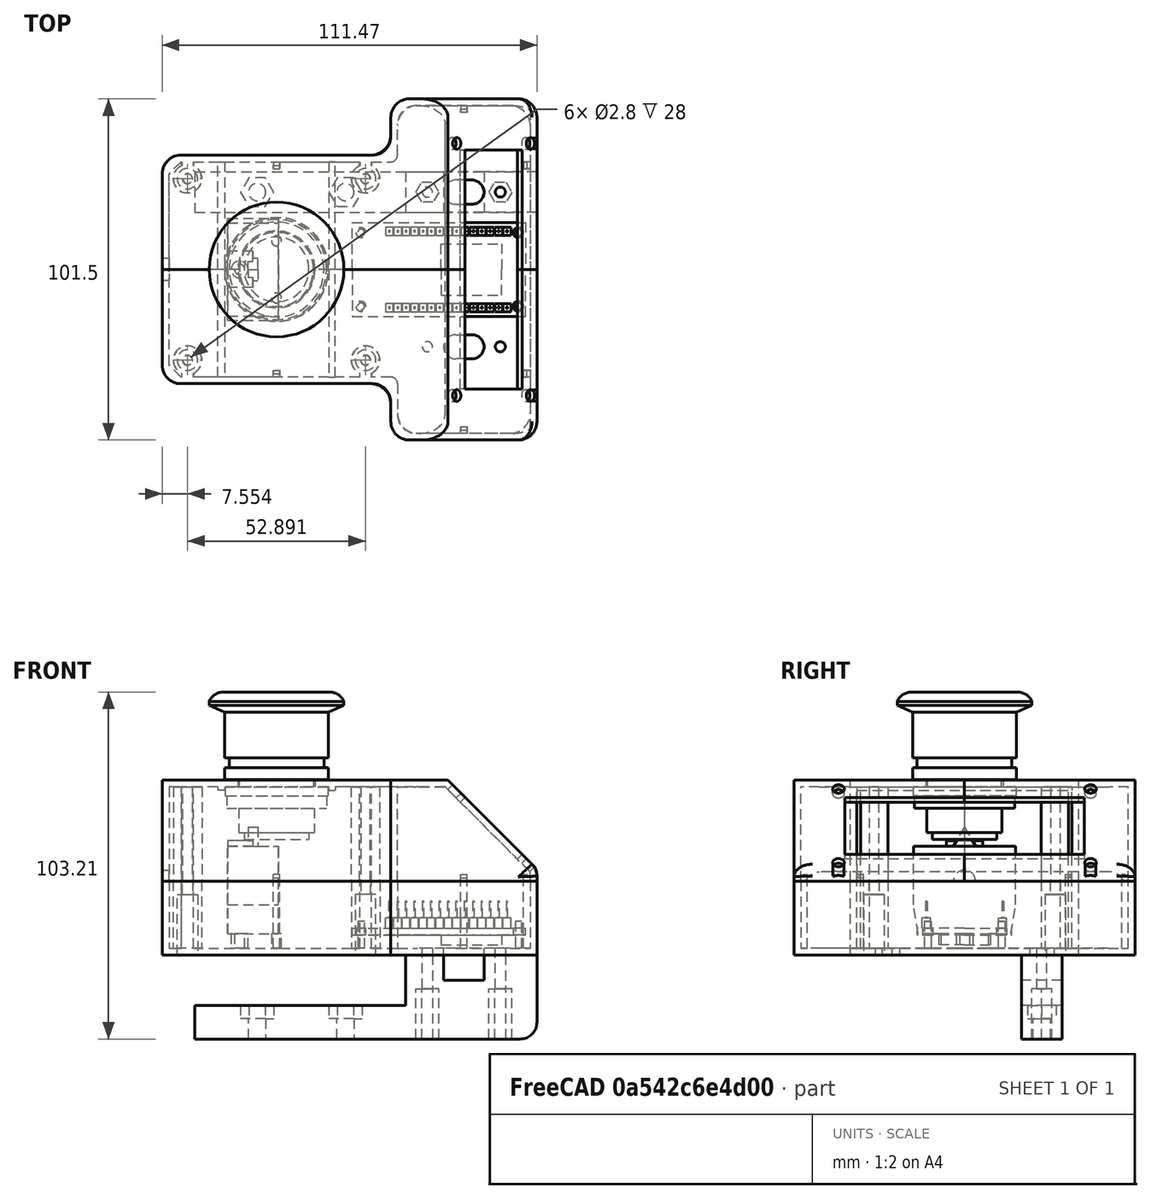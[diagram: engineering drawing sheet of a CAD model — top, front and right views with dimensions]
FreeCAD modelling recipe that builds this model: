
FCSTD DOCUMENT  (FreeCAD 0.21R33771 (Git))
Label: emergencybuttonv
License: All rights reserved
LicenseURL: https://en.wikipedia.org/wiki/All_rights_reserved
objects: Sketcher::SketchObject×35, PartDesign::Pad×16, PartDesign::Pocket×14, PartDesign::Mirrored×11, PartDesign::Body×6, PartDesign::Fillet×4, PartDesign::MultiTransform×3, Image::ImagePlane×3, PartDesign::Chamfer×3, PartDesign::Thickness×2, Mesh::Feature×1, PartDesign::Plane×1, PartDesign::Revolution×1, App::Link×1, Part::Compound×1, Part::Box×1, Part::Cut×1, PartDesign::LinearPattern×1
note: 140 computed .brp shape members not serialized (recipe doc carries the construction recipe); baked Part::Feature solids carry a one-line shape summary decoded from their .brp

FEATURE [Sketcher::SketchObject] Sketch
  FullyConstrained = false
  MapMode = 5
  Support = -> [XY_Plane]
  sketch-geometry (8):
    g0: LineSegment StartX=-34 StartY=34 StartZ=0 EndX=34 EndY=34 EndZ=0
    g1: LineSegment StartX=34 StartY=-34 StartZ=0 EndX=-34 EndY=-34 EndZ=0
    g2: LineSegment StartX=-34 StartY=-34 StartZ=0 EndX=-34 EndY=34 EndZ=0
    g3: LineSegment StartX=34 StartY=50.7535 StartZ=0 EndX=77.4691 EndY=50.7535 EndZ=0
    g4: LineSegment StartX=77.4691 StartY=50.7535 StartZ=0 EndX=77.4691 EndY=-50.7535 EndZ=0
    g5: LineSegment StartX=77.4691 StartY=-50.7535 StartZ=0 EndX=34 EndY=-50.7535 EndZ=0
    g6: LineSegment StartX=34 StartY=34 StartZ=0 EndX=34 EndY=50.7535 EndZ=0
    g7: LineSegment StartX=34 StartY=-34 StartZ=0 EndX=34 EndY=-50.7535 EndZ=0
  constraints (21):
    c: Coincident(g1,g2)
    c: Coincident(g2,g0)
    c: Horizontal(g0)
    c: Horizontal(g1)
    c: Vertical(g2)
    c: Coincident(g3,g4)
    c: Coincident(g4,g5)
    c: Horizontal(g3)
    c: Horizontal(g5)
    c: Vertical(g4)
    c: Coincident(g6,g0)
    c: Coincident(g6,g3)
    c: Vertical(g6)
    c: Coincident(g7,g1)
    c: Coincident(g7,g5)
    c: Vertical(g7)
    c: Equal(g6,g7)
    c: Symmetric(g1,g0,g-1)
    c: DistanceY(g2,g2) = 68
    c: Equal(g1,g2)
    c: Equal(g3,g5)
FEATURE [Mesh::Feature] LCD_16x2_I2C
  Placement = pos=(78,-89.5,-7) rot=(0,1,0;-0.785398rad)
FEATURE [PartDesign::Pad] Pad
  Direction = (0,0,1)
  Length = 30
  Length2 = 10
  Profile = -> Sketch
  ReferenceAxis = -> Sketch [N_Axis]
  Type = 0
FEATURE [PartDesign::Plane] DatumPlane
  AttachmentOffset = pos=(0,0,81) rot=(0,1,0;0.785398rad)
  Length = 152.683
  MapMode = 2
  Placement = pos=(0,0,81) rot=(0,1,0;0.785398rad)
  ResizeMode = 0
  Support = -> [XY_Plane]
  Width = 124.458
FEATURE [Sketcher::SketchObject] Sketch001
  FullyConstrained = false
  MapMode = 5
  Placement = pos=(0,0,81) rot=(0,1,0;0.785398rad)
  Support = -> [DatumPlane]
  sketch-geometry (4):
    g0: LineSegment StartX=17.5972 StartY=73.2272 StartZ=0 EndX=157.297 EndY=73.2272 EndZ=0
    g1: LineSegment StartX=157.297 StartY=73.2272 StartZ=0 EndX=157.297 EndY=-69.4661 EndZ=0
    g2: LineSegment StartX=157.297 StartY=-69.4661 StartZ=0 EndX=17.5972 EndY=-69.4661 EndZ=0
    g3: LineSegment StartX=17.5972 StartY=-69.4661 StartZ=0 EndX=17.5972 EndY=73.2272 EndZ=0
  constraints (8):
    c: Coincident(g0,g1)
    c: Coincident(g1,g2)
    c: Coincident(g2,g3)
    c: Coincident(g3,g0)
    c: Horizontal(g0)
    c: Horizontal(g2)
    c: Vertical(g1)
    c: Vertical(g3)
FEATURE [PartDesign::Pocket] Pocket
  BaseFeature = -> Pad
  Direction = (-0.707107,0,-0.707107)
  Length = 20
  Length2 = 5
  Profile = -> Sketch001
  ReferenceAxis = -> Sketch001 [N_Axis]
  Reversed = true
  Type = 0
FEATURE [PartDesign::Thickness] Thickness
  Base = -> Pocket [Face4]
  BaseFeature = -> Pocket
  Intersection = true
  Join = 0
  Mode = 0
  Reversed = true
  SupportTransform = false
  Value = 2
FEATURE [Sketcher::SketchObject] Sketch002
  FullyConstrained = false
  MapMode = 5
  Placement = pos=(0,0,81) rot=(0,1,0;0.785398rad)
  Support = -> [DatumPlane]
  sketch-geometry (4):
    g0: LineSegment StartX=79.3483 StartY=35.5767 StartZ=0 EndX=103.355 EndY=35.5767 EndZ=0
    g1: LineSegment StartX=103.355 StartY=35.5767 StartZ=0 EndX=103.355 EndY=-35.5767 EndZ=0
    g2: LineSegment StartX=103.355 StartY=-35.5767 StartZ=0 EndX=79.3483 EndY=-35.5767 EndZ=0
    g3: LineSegment StartX=79.3483 StartY=-35.5767 StartZ=0 EndX=79.3483 EndY=35.5767 EndZ=0
  constraints (8):
    c: Coincident(g0,g1)
    c: Coincident(g1,g2)
    c: Coincident(g2,g3)
    c: Coincident(g3,g0)
    c: Horizontal(g0)
    c: Horizontal(g2)
    c: Vertical(g1)
    c: Symmetric(g0,g2,g-1)
FEATURE [PartDesign::Pocket] Pocket001
  BaseFeature = -> Thickness
  Direction = (-0.707107,0,-0.707107)
  Length = 5
  Length2 = 5
  Profile = -> Sketch002
  ReferenceAxis = -> Sketch002 [N_Axis]
  Type = 0
FEATURE [Sketcher::SketchObject] Sketch003
  FullyConstrained = false
  MapMode = 5
  Placement = pos=(0,0,81) rot=(0,1,0;0.785398rad)
  Support = -> [DatumPlane]
  sketch-geometry (8):
    g0: LineSegment StartX=75.8332 StartY=37.5039 StartZ=0 EndX=106.819 EndY=37.5039 EndZ=0
    g1: LineSegment StartX=106.819 StartY=37.5039 StartZ=0 EndX=106.819 EndY=-37.5039 EndZ=0
    g2: LineSegment StartX=106.819 StartY=-37.5039 StartZ=0 EndX=75.8332 EndY=-37.5039 EndZ=0
    g3: LineSegment StartX=75.8332 StartY=-37.5039 StartZ=0 EndX=75.8332 EndY=37.5039 EndZ=0
    g4: Circle CenterX=75.8332 CenterY=37.5039 CenterZ=0 NormalX=0 NormalY=0 NormalZ=1 AngleXU=0 Radius=1.73847
    g5: Circle CenterX=106.819 CenterY=37.5039 CenterZ=0 NormalX=0 NormalY=0 NormalZ=1 AngleXU=0 Radius=1.73847
    g6: Circle CenterX=106.819 CenterY=-37.5039 CenterZ=0 NormalX=0 NormalY=0 NormalZ=1 AngleXU=0 Radius=1.73847
    g7: Circle CenterX=75.8332 CenterY=-37.5039 CenterZ=0 NormalX=0 NormalY=0 NormalZ=1 AngleXU=0 Radius=1.73847
  constraints (15):
    c: Coincident(g0,g1)
    c: Coincident(g1,g2)
    c: Coincident(g2,g3)
    c: Coincident(g3,g0)
    c: Horizontal(g0)
    c: Horizontal(g2)
    c: Vertical(g1)
    c: Symmetric(g2,g0,g-1)
    c: Coincident(g4,g0)
    c: Coincident(g5,g0)
    c: Coincident(g6,g1)
    c: Coincident(g7,g2)
    c: Equal(g4,g5)
    c: Equal(g5,g6)
    c: Equal(g6,g7)
FEATURE [PartDesign::Pocket] Pocket002
  BaseFeature = -> Pocket001
  Direction = (-0.707107,0,-0.707107)
  Length = 7
  Length2 = 5
  Profile = -> Sketch003
  ReferenceAxis = -> Sketch003 [N_Axis]
  Type = 0
FEATURE [Sketcher::SketchObject] Sketch004
  FullyConstrained = true
  MapMode = 5
  Support = -> [XY_Plane]
  sketch-geometry (1):
    g0: Circle CenterX=0 CenterY=0 CenterZ=0 NormalX=0 NormalY=0 NormalZ=1 AngleXU=0 Radius=11
  constraints (2):
    c: Coincident(g0,g-1)
    c: Diameter(g0) = 22
FEATURE [PartDesign::Pocket] Pocket003
  BaseFeature = -> Pocket002
  Direction = (0,0,-1)
  Length = 5
  Length2 = 5
  Midplane = true
  Profile = -> Sketch004
  ReferenceAxis = -> Sketch004 [N_Axis]
  Type = 1
FEATURE [Sketcher::SketchObject] Sketch005
  ExternalGeometry = -> [Sketch]
  FullyConstrained = false
  MapMode = 5
  Support = -> [XY_Plane]
  sketch-geometry (4):
    g0: LineSegment StartX=24.6956 StartY=32 StartZ=0 EndX=28.1956 EndY=32 EndZ=0
    g1: LineSegment StartX=28.1956 StartY=32 StartZ=0 EndX=28.1956 EndY=30.873 EndZ=0
    g2: LineSegment StartX=24.6956 StartY=30.873 StartZ=0 EndX=24.6956 EndY=32 EndZ=0
    g3: ArcOfCircle CenterX=26.4456 CenterY=27 CenterZ=0 NormalX=0 NormalY=0 NormalZ=1 AngleXU=0 Radius=4.25 StartAngle=1.99519 EndAngle=7.42959
  constraints (12):
    c: Coincident(g0,g1)
    c: Coincident(g2,g0)
    c: Horizontal(g0)
    c: Vertical(g1)
    c: Vertical(g2)
    c: Coincident(g3,g2)
    c: Coincident(g3,g1)
    c: Equal(g1,g2)
    c: Diameter(g3) = 8.5
    c: Distance(g0) = 3.5
    c: DistanceY(g3,g0) = 5
    c: DistanceY(g0,g-3) = 2
FEATURE [PartDesign::Pad] Pad001
  BaseFeature = -> Pocket003
  Direction = (0,0,1)
  Length = 28
  Length2 = 10
  Profile = -> Sketch005
  ReferenceAxis = -> Sketch005 [N_Axis]
  Type = 0
FEATURE [Sketcher::SketchObject] Sketch006
  ExternalGeometry = -> [Sketch005]
  FullyConstrained = true
  MapMode = 5
  Support = -> [XY_Plane]
  sketch-geometry (1):
    g0: Circle CenterX=26.4456 CenterY=27 CenterZ=0 NormalX=0 NormalY=0 NormalZ=1 AngleXU=0 Radius=1.4
  constraints (2):
    c: Coincident(g0,g-3)
    c: Diameter(g0) = 2.8
FEATURE [PartDesign::Pocket] Pocket004
  BaseFeature = -> Pad001
  Direction = (0,0,-1)
  Length = 28
  Length2 = 5
  Profile = -> Sketch006
  ReferenceAxis = -> Sketch006 [N_Axis]
  Reversed = true
  Type = 0
FEATURE [PartDesign::Mirrored] Mirrored
  MirrorPlane = -> Sketch006 [V_Axis]
FEATURE [PartDesign::Mirrored] Mirrored001
  MirrorPlane = -> Sketch006 [H_Axis]
FEATURE [PartDesign::MultiTransform] MultiTransform
  BaseFeature = -> Pocket004
  Originals = -> [Pad001,Pocket004]
  Transformations = -> [Mirrored,Mirrored001]
FEATURE [Sketcher::SketchObject] Sketch007
  FullyConstrained = false
  MapMode = 5
  Support = -> [XY_Plane001]
  sketch-geometry (8):
    g0: LineSegment StartX=-34 StartY=34 StartZ=0 EndX=34 EndY=34 EndZ=0
    g1: LineSegment StartX=34 StartY=-34 StartZ=0 EndX=-34 EndY=-34 EndZ=0
    g2: LineSegment StartX=-34 StartY=-34 StartZ=0 EndX=-34 EndY=34 EndZ=0
    g3: LineSegment StartX=34 StartY=50.7535 StartZ=0 EndX=77.4691 EndY=50.7535 EndZ=0
    g4: LineSegment StartX=77.4691 StartY=50.7535 StartZ=0 EndX=77.4691 EndY=-50.7535 EndZ=0
    g5: LineSegment StartX=77.4691 StartY=-50.7535 StartZ=0 EndX=34 EndY=-50.7535 EndZ=0
    g6: LineSegment StartX=34 StartY=34 StartZ=0 EndX=34 EndY=50.7535 EndZ=0
    g7: LineSegment StartX=34 StartY=-34 StartZ=0 EndX=34 EndY=-50.7535 EndZ=0
  constraints (21):
    c: Coincident(g1,g2)
    c: Coincident(g2,g0)
    c: Horizontal(g0)
    c: Horizontal(g1)
    c: Vertical(g2)
    c: Coincident(g3,g4)
    c: Coincident(g4,g5)
    c: Horizontal(g3)
    c: Horizontal(g5)
    c: Vertical(g4)
    c: Coincident(g6,g0)
    c: Coincident(g6,g3)
    c: Vertical(g6)
    c: Coincident(g7,g1)
    c: Coincident(g7,g5)
    c: Vertical(g7)
    c: Equal(g6,g7)
    c: Symmetric(g1,g0,g-1)
    c: DistanceY(g2,g2) = 68
    c: Equal(g1,g2)
    c: Equal(g3,g5)
FEATURE [PartDesign::Pad] Pad002
  Direction = (0,0,1)
  Length = 22
  Length2 = 10
  Profile = -> Sketch007
  ReferenceAxis = -> Sketch007 [N_Axis]
  Type = 0
FEATURE [Sketcher::SketchObject] Sketch012
  ExternalGeometry = -> [Sketch007]
  FullyConstrained = false
  MapMode = 5
  Support = -> [XY_Plane001]
  sketch-geometry (4):
    g0: LineSegment StartX=24.7653 StartY=32 StartZ=0 EndX=28.2653 EndY=32 EndZ=0
    g1: LineSegment StartX=28.2653 StartY=32 StartZ=0 EndX=28.2653 EndY=30.873 EndZ=0
    g2: LineSegment StartX=24.7653 StartY=30.873 StartZ=0 EndX=24.7653 EndY=32 EndZ=0
    g3: ArcOfCircle CenterX=26.5153 CenterY=27 CenterZ=0 NormalX=0 NormalY=0 NormalZ=1 AngleXU=0 Radius=4.25 StartAngle=1.99519 EndAngle=7.42959
  constraints (12):
    c: Coincident(g0,g1)
    c: Coincident(g2,g0)
    c: Horizontal(g0)
    c: Vertical(g1)
    c: Vertical(g2)
    c: Coincident(g3,g2)
    c: Coincident(g3,g1)
    c: Equal(g1,g2)
    c: Diameter(g3) = 8.5
    c: Distance(g0) = 3.5
    c: DistanceY(g3,g0) = 5
    c: DistanceY(g0,g-3) = 2
FEATURE [Sketcher::SketchObject] Sketch013
  ExternalGeometry = -> [Sketch012]
  FullyConstrained = true
  MapMode = 5
  Support = -> [XY_Plane001]
  sketch-geometry (1):
    g0: Circle CenterX=26.5153 CenterY=27 CenterZ=0 NormalX=0 NormalY=0 NormalZ=1 AngleXU=0 Radius=1.5
  constraints (2):
    c: Coincident(g0,g-3)
    c: Diameter(g0) = 3
FEATURE [PartDesign::Thickness] Thickness001
  Base = -> Pad002 [Face10]
  BaseFeature = -> Pad002
  Intersection = true
  Join = 0
  Mode = 0
  Reversed = true
  SupportTransform = false
  Value = 2
FEATURE [PartDesign::Pad] Pad003
  BaseFeature = -> Thickness001
  Direction = (0,0,1)
  Length = 22
  Length2 = 10
  Profile = -> Sketch012
  ReferenceAxis = -> Sketch012 [N_Axis]
  Type = 0
FEATURE [PartDesign::Pocket] Pocket009
  BaseFeature = -> Pad003
  Direction = (0,0,-1)
  Length = 32
  Length2 = 5
  Profile = -> Sketch013
  ReferenceAxis = -> Sketch013 [N_Axis]
  Reversed = true
  Type = 0
FEATURE [Sketcher::SketchObject] Sketch014
  ExternalGeometry = -> [Sketch012]
  FullyConstrained = true
  MapMode = 5
  Support = -> [XY_Plane001]
  sketch-geometry (1):
    g0: Circle CenterX=26.5153 CenterY=27 CenterZ=0 NormalX=0 NormalY=0 NormalZ=1 AngleXU=0 Radius=3.05
  constraints (2):
    c: Coincident(g0,g-3)
    c: Diameter(g0) = 6.1
FEATURE [PartDesign::Pocket] Pocket010
  BaseFeature = -> Pocket009
  Direction = (0,0,-1)
  Length = 18
  Length2 = 5
  Profile = -> Sketch014
  ReferenceAxis = -> Sketch014 [N_Axis]
  Reversed = true
  Type = 0
FEATURE [PartDesign::Mirrored] Mirrored002
  MirrorPlane = -> Sketch012 [V_Axis]
FEATURE [PartDesign::Mirrored] Mirrored003
  MirrorPlane = -> Sketch012 [H_Axis]
FEATURE [PartDesign::MultiTransform] MultiTransform001
  BaseFeature = -> Pocket010
  Originals = -> [Pad003,Pocket009,Pocket010]
  Transformations = -> [Mirrored002,Mirrored003]
FEATURE [Sketcher::SketchObject] Sketch015
  FullyConstrained = true
  MapMode = 5
  Support = -> [XY_Plane001]
  sketch-geometry (5):
    g0: Circle CenterX=0 CenterY=0 CenterZ=0 NormalX=0 NormalY=0 NormalZ=1 AngleXU=0 Radius=11
    g1: Circle CenterX=-11 CenterY=0 CenterZ=0 NormalX=0 NormalY=0 NormalZ=1 AngleXU=0 Radius=1.5
    g2: Circle CenterX=-11 CenterY=0 CenterZ=0 NormalX=0 NormalY=0 NormalZ=1 AngleXU=0 Radius=2.5
    g3: Circle CenterX=9e-16 CenterY=8.5 CenterZ=0 NormalX=0 NormalY=0 NormalZ=1 AngleXU=0 Radius=1.5
    g4: Circle CenterX=9e-16 CenterY=-8.5 CenterZ=0 NormalX=0 NormalY=0 NormalZ=1 AngleXU=0 Radius=1.5
  constraints (12):
    c: Coincident(g0,g-1)
    c: Diameter(g0) = 22
    c: PointOnObject(g1,g0)
    c: PointOnObject(g1,g-1)
    c: Coincident(g2,g1)
    c: Diameter(g1) = 3
    c: Diameter(g2) = 5
    c: Symmetric(g4,g3,g-1)
    c: Equal(g3,g4)
    c: Equal(g4,g1)
    c: DistanceX(g1,g4) = 11
    c: DistanceY(g4,g3) = 17
FEATURE [PartDesign::Pad] Pad004
  BaseFeature = -> MultiTransform001
  Direction = (0,0,1)
  Length = 6.3
  Length2 = 10
  Profile = -> Sketch015
  ReferenceAxis = -> Sketch015 [N_Axis]
  Type = 0
FEATURE [Sketcher::SketchObject] Sketch016
  ExternalGeometry = -> [Sketch007]
  FullyConstrained = true
  MapMode = 5
  Support = -> [XY_Plane001]
  sketch-geometry (12):
    g0: LineSegment StartX=-1 StartY=32 StartZ=0 EndX=1 EndY=32 EndZ=0
    g1: LineSegment StartX=1 StartY=32 StartZ=0 EndX=1 EndY=30 EndZ=0
    g2: LineSegment StartX=1 StartY=30 StartZ=0 EndX=-1 EndY=30 EndZ=0
    g3: LineSegment StartX=-1 StartY=30 StartZ=0 EndX=-1 EndY=32 EndZ=0
    g4: LineSegment StartX=54.7341 StartY=48.7535 StartZ=0 EndX=56.7341 EndY=48.7535 EndZ=0
    g5: LineSegment StartX=56.7341 StartY=48.7535 StartZ=0 EndX=56.7341 EndY=46.7535 EndZ=0
    g6: LineSegment StartX=56.7341 StartY=46.7535 StartZ=0 EndX=54.7341 EndY=46.7535 EndZ=0
    g7: LineSegment StartX=54.7341 StartY=46.7535 StartZ=0 EndX=54.7341 EndY=48.7535 EndZ=0
    g8: LineSegment StartX=73.4691 StartY=32 StartZ=0 EndX=75.4691 EndY=32 EndZ=0
    g9: LineSegment StartX=75.4691 StartY=32 StartZ=0 EndX=75.4691 EndY=30 EndZ=0
    g10: LineSegment StartX=75.4691 StartY=30 StartZ=0 EndX=73.4691 EndY=30 EndZ=0
    g11: LineSegment StartX=73.4691 StartY=30 StartZ=0 EndX=73.4691 EndY=32 EndZ=0
  constraints (36):
    c: Coincident(g0,g1)
    c: Coincident(g1,g2)
    c: Coincident(g2,g3)
    c: Coincident(g3,g0)
    c: Horizontal(g0)
    c: Vertical(g1)
    c: Vertical(g3)
    c: Coincident(g4,g5)
    c: Coincident(g5,g6)
    c: Coincident(g6,g7)
    c: Coincident(g7,g4)
    c: Horizontal(g4)
    c: Horizontal(g6)
    c: Vertical(g5)
    c: Vertical(g7)
    c: DistanceY(g4,g-8) = 2
    c: Equal(g4,g5)
    c: Equal(g5,g1)
    c: Equal(g1,g0)
    c: DistanceY(g0,g-9) = 2
    c: Symmetric(g1,g2,g-2)
    c: DistanceX(g4,g4) = 2
    c: DistanceX(g-8,g-8) = 43.4691
    c: DistanceX(g4,g-8) = 20.735
    c: Coincident(g8,g9)
    c: Coincident(g9,g10)
    c: Coincident(g10,g11)
    c: Coincident(g11,g8)
    c: Horizontal(g8)
    c: Horizontal(g10)
    c: Vertical(g9)
    c: Vertical(g11)
    c: Equal(g10,g11)
    c: Equal(g11,g1)
    c: DistanceX(g8,g-8) = 2
    c: DistanceY(g8,g-9) = 2
FEATURE [PartDesign::Pad] Pad005
  BaseFeature = -> Pad004
  Direction = (0,0,1)
  Length = 24
  Length2 = 10
  Profile = -> Sketch016
  ReferenceAxis = -> Sketch016 [N_Axis]
  Type = 0
FEATURE [PartDesign::Mirrored] Mirrored004
  BaseFeature = -> Pad005
  MirrorPlane = -> XZ_Plane001
  Originals = -> [Pad005]
FEATURE [Sketcher::SketchObject] Sketch017
  ExternalGeometry = -> [Sketch007]
  FullyConstrained = false
  MapMode = 5
  Support = -> [XY_Plane001]
  sketch-geometry (3):
    g0: Circle CenterX=25.1596 CenterY=10.985 CenterZ=0 NormalX=0 NormalY=0 NormalZ=1 AngleXU=0 Radius=1
    g1: Circle CenterX=71.9791 CenterY=10.985 CenterZ=0 NormalX=0 NormalY=0 NormalZ=1 AngleXU=0 Radius=1
    g2: LineSegment StartX=71.9791 StartY=10.985 StartZ=0 EndX=25.1596 EndY=10.985 EndZ=0
  constraints (5):
    c: Equal(g1,g0)
    c: Coincident(g2,g1)
    c: Coincident(g2,g0)
    c: Horizontal(g2)
    c: Diameter(g1) = 2
FEATURE [PartDesign::Pad] Pad006
  BaseFeature = -> Mirrored004
  Direction = (0,0,1)
  Length = 10
  Length2 = 10
  Profile = -> Sketch017
  ReferenceAxis = -> Sketch017 [N_Axis]
  Type = 0
FEATURE [Sketcher::SketchObject] Sketch018
  ExternalGeometry = -> [Sketch007]
  FullyConstrained = true
  MapMode = 5
  Support = -> [XY_Plane001]
  sketch-geometry (10):
    g0: ArcOfCircle CenterX=53.3345 CenterY=23 CenterZ=0 NormalX=0 NormalY=0 NormalZ=1 AngleXU=0 Radius=3.6 StartAngle=1.5708 EndAngle=4.71239
    g1: ArcOfCircle CenterX=58.1345 CenterY=23 CenterZ=0 NormalX=0 NormalY=0 NormalZ=1 AngleXU=0 Radius=3.6 StartAngle=4.71239 EndAngle=7.85398
    g2: LineSegment StartX=53.3345 StartY=19.4 StartZ=0 EndX=58.1345 EndY=19.4 EndZ=0
    g3: LineSegment StartX=58.1345 StartY=26.6 StartZ=0 EndX=53.3345 EndY=26.6 EndZ=0
    g4: LineSegment StartX=49.7345 StartY=26.6 StartZ=0 EndX=61.7345 EndY=26.6 EndZ=0
    g5: LineSegment StartX=61.7345 StartY=26.6 StartZ=0 EndX=61.7345 EndY=19.4 EndZ=0
    g6: LineSegment StartX=61.7345 StartY=19.4 StartZ=0 EndX=49.7345 EndY=19.4 EndZ=0
    g7: LineSegment StartX=49.7345 StartY=19.4 StartZ=0 EndX=49.7345 EndY=26.6 EndZ=0
    g8: LineSegment StartX=58.1345 StartY=23 StartZ=0 EndX=77.4691 EndY=50.7535 EndZ=0
    g9: LineSegment StartX=53.3345 StartY=23 StartZ=0 EndX=34 EndY=50.7535 EndZ=0
  constraints (26):
    c: Tangent(g0,g2) = -1.5708
    c: Tangent(g2,g1) = -1.5708
    c: Tangent(g1,g3) = -1.5708
    c: Tangent(g3,g0) = -1.5708
    c: Equal(g0,g1)
    c: Horizontal(g2)
    c: Coincident(g4,g5)
    c: Coincident(g5,g6)
    c: Coincident(g6,g7)
    c: Coincident(g7,g4)
    c: Horizontal(g4)
    c: Horizontal(g6)
    c: Vertical(g5)
    c: Vertical(g7)
    c: Tangent(g5,g1)
    c: Tangent(g7,g0)
    c: PointOnObject(g0,g4)
    c: PointOnObject(g0,g6)
    c: DistanceY(g5,g5) = 7.2
    c: DistanceX(g6,g6) = 12
    c: Coincident(g8,g1)
    c: Coincident(g8,g-5)
    c: Coincident(g9,g0)
    c: Coincident(g9,g-5)
    c: Equal(g8,g9)
    c: DistanceY(g-1,g1) = 23
FEATURE [PartDesign::Pocket] Pocket011
  BaseFeature = -> Pad006
  Direction = (0,0,-1)
  Length = 5
  Length2 = 5
  Midplane = true
  Profile = -> Sketch018
  ReferenceAxis = -> Sketch018 [N_Axis]
  Type = 1
FEATURE [Sketcher::SketchObject] Sketch019
  ExternalGeometry = -> [Sketch013,Sketch018]
  FullyConstrained = false
  MapMode = 5
  Support = -> [XY_Plane001]
  sketch-geometry (6):
    g0: Circle CenterX=66.5863 CenterY=23 CenterZ=0 NormalX=0 NormalY=0 NormalZ=1 AngleXU=0 Radius=1.5
    g1: Circle CenterX=44.8828 CenterY=23 CenterZ=0 NormalX=0 NormalY=0 NormalZ=1 AngleXU=0 Radius=1.5
    g2: LineSegment StartX=44.8828 StartY=23 StartZ=0 EndX=66.5863 EndY=23 EndZ=0
    g3: LineSegment StartX=53.3345 StartY=26.6 StartZ=0 EndX=58.1345 EndY=19.4 EndZ=0
    g4: LineSegment StartX=53.3345 StartY=19.4 StartZ=0 EndX=58.1345 EndY=26.6 EndZ=0
    g5: GeomPoint X=55.7345 Y=23 Z=0
  constraints (12):
    c: Equal(g1,g-3)
    c: Equal(g-3,g0)
    c: Coincident(g2,g1)
    c: Coincident(g2,g0)
    c: PointOnObject(g-5,g2)
    c: Coincident(g3,g-4)
    c: Coincident(g3,g-5)
    c: Coincident(g4,g-4)
    c: Coincident(g4,g-5)
    c: Symmetric(g0,g1,g5)
    c: PointOnObject(g-4,g2)
    c: PointOnObject(g5,g3)
FEATURE [PartDesign::Pocket] Pocket012
  BaseFeature = -> Pocket011
  Direction = (0,0,-1)
  Length = 5
  Length2 = 5
  Midplane = true
  Profile = -> Sketch019
  ReferenceAxis = -> Sketch019 [N_Axis]
  Type = 1
FEATURE [PartDesign::Mirrored] Mirrored005
  BaseFeature = -> Pocket012
  MirrorPlane = -> Sketch017 [H_Axis]
  Originals = -> [Pad006,Pocket011,Pocket012]
FEATURE [Image::ImagePlane] button
  Placement = pos=(7,0,0) rot=(1,0,0;1.5708rad)
  XSize = 74.3051
  YSize = 111.458
FEATURE [Sketcher::SketchObject] Sketch020
  FullyConstrained = false
  MapMode = 5
  Placement = pos=(0,0,0) rot=(1,0,0;1.5708rad)
  Support = -> [XZ_Plane002]
  sketch-geometry (21):
    g0: LineSegment StartX=0 StartY=21.715 StartZ=0 EndX=-15.8355 EndY=21.715 EndZ=0
    g1: ArcOfCircle CenterX=-15.8355 CenterY=17.1339 CenterZ=0 NormalX=0 NormalY=0 NormalZ=1 AngleXU=0 Radius=4.58113 StartAngle=1.5708 EndAngle=2.73807
    g2: LineSegment StartX=-20.0486 StartY=18.9327 StartZ=0 EndX=-20.0486 EndY=17.7137 EndZ=0
    g3: LineSegment StartX=-20.0486 StartY=17.7137 StartZ=0 EndX=-15.4608 EndY=15.773 EndZ=0
    g4: LineSegment StartX=-15.4608 StartY=15.773 StartZ=0 EndX=-15.4608 EndY=2.19549 EndZ=0
    g5: LineSegment StartX=-15.4608 StartY=2.19549 StartZ=0 EndX=-14.0996 EndY=2.19549 EndZ=0
    g6: LineSegment StartX=-14.0996 StartY=2.19549 StartZ=0 EndX=-14.0996 EndY=-0.733472 EndZ=0
    g7: LineSegment StartX=-14.0996 StartY=-0.733472 StartZ=0 EndX=-15.4212 EndY=-0.733472 EndZ=0
    g8: LineSegment StartX=-15.4212 StartY=-0.733472 StartZ=0 EndX=-15.4212 EndY=-4.39312 EndZ=0
    g9: LineSegment StartX=-15.4212 StartY=-4.39312 StartZ=0 EndX=-11.4574 EndY=-4.39312 EndZ=0
    g10: LineSegment StartX=-11.4574 StartY=-4.39312 StartZ=0 EndX=-11.4574 EndY=-6.5 EndZ=0
    g11: LineSegment StartX=-11.4574 StartY=-6.5 StartZ=0 EndX=-15.3359 EndY=-6.5 EndZ=0
    g12: LineSegment StartX=-15.3359 StartY=-6.5 StartZ=0 EndX=-15.3359 EndY=-9.10006 EndZ=0
    g13: LineSegment StartX=-15.3359 StartY=-9.10006 StartZ=0 EndX=-14.8733 EndY=-9.10006 EndZ=0
    g14: LineSegment StartX=-14.8733 StartY=-9.10006 StartZ=0 EndX=-14.8733 EndY=-12.8352 EndZ=0
    g15: LineSegment StartX=-14.8733 StartY=-12.8352 StartZ=0 EndX=-11.186 EndY=-12.8352 EndZ=0
    g16: LineSegment StartX=-11.186 StartY=-12.8352 StartZ=0 EndX=-11.186 EndY=-20.0552 EndZ=0
    g17: LineSegment StartX=-11.186 StartY=-20.0552 StartZ=0 EndX=-9.63472 EndY=-20.0944 EndZ=0
    g18: LineSegment StartX=-9.63472 StartY=-20.0944 StartZ=0 EndX=-9.63472 EndY=-22.0683 EndZ=0
    g19: LineSegment StartX=-9.63472 StartY=-22.0683 StartZ=0 EndX=0 EndY=-22.0683 EndZ=0
    g20: LineSegment StartX=0 StartY=-22.0683 StartZ=0 EndX=0 EndY=21.715 EndZ=0
  constraints (40):
    c: PointOnObject(g0,g-2)
    c: Horizontal(g0)
    c: Tangent(g0,g1) = -1.5708
    c: Coincident(g1,g2)
    c: Vertical(g2)
    c: Coincident(g2,g3)
    c: Coincident(g3,g4)
    c: Vertical(g4)
    c: Coincident(g4,g5)
    c: Horizontal(g5)
    c: Coincident(g5,g6)
    c: Vertical(g6)
    c: Coincident(g6,g7)
    c: Horizontal(g7)
    c: Coincident(g7,g8)
    c: Vertical(g8)
    c: Coincident(g8,g9)
    c: Horizontal(g9)
    c: Coincident(g9,g10)
    c: Vertical(g10)
    c: Coincident(g10,g11)
    c: Horizontal(g11)
    c: Coincident(g11,g12)
    c: Vertical(g12)
    c: Coincident(g12,g13)
    c: Horizontal(g13)
    c: Coincident(g13,g14)
    c: Vertical(g14)
    c: Coincident(g14,g15)
    c: Horizontal(g15)
    c: Coincident(g15,g16)
    c: Vertical(g16)
    c: Coincident(g16,g17)
    c: Coincident(g17,g18)
    c: Vertical(g18)
    c: Coincident(g18,g19)
    c: Horizontal(g19)
    c: Coincident(g19,g20)
    c: Coincident(g20,g0)
    c: Vertical(g20)
FEATURE [PartDesign::Revolution] Revolution
  Angle = 360
  Axis = (0,-2e-16,1)
  Base = (0,0,0)
  Placement = pos=(0,0,0) rot=(1,0,0;1.5708rad)
  Profile = -> Sketch020
  ReferenceAxis = -> Sketch020 [V_Axis]
FEATURE [PartDesign::Body] Body002  label="MushroomPressed"
  Group = -> [Sketch020,Revolution]
  Origin = -> Origin002
  Placement = pos=(0,0,34.5) rot=(0,0,1;0rad)
  Tip = -> Revolution
FEATURE [App::Link] Body_CutLink
  LinkTransform = true
  LinkedObject = -> Body
FEATURE [Part::Compound] SectionCutCompound
  Links = -> [Body_CutLink]
FEATURE [Part::Box] SectionCutBoxY
  AttacherType = Attacher::AttachEngine3D
  Height = 31
  Length = 112.469
  Placement = pos=(-34.5,-102.507,-0.5) rot=(0,0,1;0rad)
  Width = 102.507
FEATURE [Part::Cut] SectionCutY
  Base = -> SectionCutCompound
  Tool = -> SectionCutBoxY
FEATURE [Image::ImagePlane] swithch
  Placement = pos=(-90,6.75,0) rot=(0,1,0;1.5708rad)
  XSize = 107.771
  YSize = 71.8474
FEATURE [Sketcher::SketchObject] Sketch021
  FullyConstrained = false
  MapMode = 5
  Placement = pos=(0,0,0) rot=(0.57735,0.57735,0.57735;2.0944rad)
  Support = -> [YZ_Plane003]
  sketch-geometry (5):
    g0: LineSegment StartX=0 StartY=-11.6653 StartZ=0 EndX=-13.8324 EndY=-11.6653 EndZ=0
    g1: LineSegment StartX=-13.8324 StartY=-11.6653 StartZ=0 EndX=-15.1866 EndY=-3.04616 EndZ=0
    g2: LineSegment StartX=-15.1866 StartY=-3.04616 StartZ=0 EndX=-15.1866 EndY=14.3347 EndZ=0
    g3: LineSegment StartX=-15.1866 StartY=14.3347 StartZ=0 EndX=0 EndY=14.3347 EndZ=0
    g4: LineSegment StartX=0 StartY=14.3347 StartZ=0 EndX=0 EndY=-11.6653 EndZ=0
  constraints (11):
    c: PointOnObject(g0,g-2)
    c: Horizontal(g0)
    c: Coincident(g0,g1)
    c: Coincident(g1,g2)
    c: Vertical(g2)
    c: Coincident(g2,g3)
    c: Horizontal(g3)
    c: PointOnObject(g3,g-2)
    c: Coincident(g4,g3)
    c: Coincident(g4,g0)
    c: DistanceY(g4,g4) = 26
FEATURE [PartDesign::Pad] Pad007
  Direction = (1,-2e-16,3e-16)
  Length = 15
  Length2 = 10
  Midplane = true
  Placement = pos=(0,0,0) rot=(0.57735,0.57735,0.57735;2.0944rad)
  Profile = -> Sketch021
  ReferenceAxis = -> Sketch021 [N_Axis]
  Type = 0
FEATURE [Sketcher::SketchObject] Sketch022
  ExternalGeometry = -> [Sketch021]
  FullyConstrained = false
  MapMode = 5
  Placement = pos=(0,0,0) rot=(0.57735,0.57735,0.57735;2.0944rad)
  Support = -> [YZ_Plane003]
  sketch-geometry (4):
    g0: LineSegment StartX=-5.41796 StartY=14.3347 StartZ=0 EndX=0 EndY=14.3347 EndZ=0
    g1: LineSegment StartX=0 StartY=14.3347 StartZ=0 EndX=0 EndY=15.9851 EndZ=0
    g2: LineSegment StartX=0 StartY=15.9851 StartZ=0 EndX=-5.41796 EndY=15.9851 EndZ=0
    g3: LineSegment StartX=-5.41796 StartY=15.9851 StartZ=0 EndX=-5.41796 EndY=14.3347 EndZ=0
  constraints (10):
    c: Coincident(g0,g1)
    c: Coincident(g1,g2)
    c: Coincident(g2,g3)
    c: Coincident(g3,g0)
    c: Horizontal(g0)
    c: Horizontal(g2)
    c: Vertical(g1)
    c: Vertical(g3)
    c: PointOnObject(g0,g-3)
    c: PointOnObject(g1,g-2)
FEATURE [PartDesign::Pad] Pad008
  BaseFeature = -> Pad007
  Direction = (1,-2e-16,3e-16)
  Length = 7.5
  Length2 = 10
  Placement = pos=(0,0,0) rot=(0.57735,0.57735,0.57735;2.0944rad)
  Profile = -> Sketch022
  ReferenceAxis = -> Sketch022 [N_Axis]
  Reversed = true
  Type = 0
FEATURE [Sketcher::SketchObject] Sketch023
  ExternalGeometry = -> [Sketch022,Sketch021]
  FullyConstrained = false
  MapMode = 5
  Placement = pos=(0,0,0) rot=(0.57735,0.57735,0.57735;2.0944rad)
  Support = -> [YZ_Plane003]
  sketch-geometry (3):
    g0: LineSegment StartX=0 StartY=20.0793 StartZ=0 EndX=-3.37704 EndY=14.3347 EndZ=0
    g1: LineSegment StartX=-3.37704 StartY=14.3347 StartZ=0 EndX=0 EndY=14.3347 EndZ=0
    g2: LineSegment StartX=0 StartY=14.3347 StartZ=0 EndX=0 EndY=20.0793 EndZ=0
  constraints (6):
    c: PointOnObject(g0,g-2)
    c: PointOnObject(g0,g-4)
    c: Coincident(g0,g1)
    c: Coincident(g1,g-4)
    c: Coincident(g1,g2)
    c: Coincident(g2,g0)
FEATURE [PartDesign::Pad] Pad009
  BaseFeature = -> Pad008
  Direction = (1,-2e-16,3e-16)
  Length = 3
  Length2 = 10
  Midplane = true
  Placement = pos=(0,0,0) rot=(0.57735,0.57735,0.57735;2.0944rad)
  Profile = -> Sketch023
  ReferenceAxis = -> Sketch023 [N_Axis]
  Type = 0
FEATURE [PartDesign::Mirrored] Mirrored006
  BaseFeature = -> Pad009
  MirrorPlane = -> Sketch021 [V_Axis]
  Originals = -> [Pad007,Pad008,Pad009]
  Placement = pos=(0,0,0) rot=(0.57735,0.57735,0.57735;2.0944rad)
FEATURE [PartDesign::Body] Body003  label="Switch"
  Group = -> [Sketch021,Pad007,Sketch022,Pad008,Sketch023,Pad009,Mirrored006]
  Origin = -> Origin003
  Placement = pos=(-7,0,-4) rot=(0,0,1;0rad)
  Tip = -> Mirrored006
FEATURE [Image::ImagePlane] esp
  Placement = pos=(0,0,0) rot=(0,0,1;1.5708rad)
  XSize = 79.5024
  YSize = 73.9557
FEATURE [Sketcher::SketchObject] Sketch024
  FullyConstrained = false
  MapMode = 5
  Support = -> [XY_Plane004]
  sketch-geometry (7):
    g0: LineSegment StartX=-26.4367 StartY=14 StartZ=0 EndX=25.0633 EndY=14 EndZ=0
    g1: LineSegment StartX=25.0633 StartY=14 StartZ=0 EndX=25.0633 EndY=0 EndZ=0
    g2: LineSegment StartX=25.0633 StartY=0 StartZ=0 EndX=-26.4367 EndY=0 EndZ=0
    g3: LineSegment StartX=-26.4367 StartY=0 StartZ=0 EndX=-26.4367 EndY=14 EndZ=0
    g4: Circle CenterX=22.9502 CenterY=10.9692 CenterZ=0 NormalX=0 NormalY=0 NormalZ=1 AngleXU=0 Radius=1.5221
    g5: Circle CenterX=-23.8878 CenterY=10.9692 CenterZ=0 NormalX=0 NormalY=0 NormalZ=1 AngleXU=0 Radius=1.47889
    g6: LineSegment StartX=-23.8878 StartY=10.9692 StartZ=0 EndX=22.9502 EndY=10.9692 EndZ=0
  constraints (14):
    c: Coincident(g0,g1)
    c: Coincident(g1,g2)
    c: Coincident(g2,g3)
    c: Coincident(g3,g0)
    c: Horizontal(g0)
    c: Horizontal(g2)
    c: Vertical(g1)
    c: Vertical(g3)
    c: PointOnObject(g1,g-1)
    c: Coincident(g6,g5)
    c: Coincident(g6,g4)
    c: Horizontal(g6)
    c: DistanceY(g1,g1) = 14
    c: DistanceX(g0,g0) = 51.5
FEATURE [PartDesign::Pad] Pad010
  Direction = (0,0,1)
  Length = 2
  Length2 = 10
  Profile = -> Sketch024
  ReferenceAxis = -> Sketch024 [N_Axis]
  Type = 0
FEATURE [Sketcher::SketchObject] Sketch025
  FullyConstrained = false
  MapMode = 5
  Support = -> [XY_Plane004]
  sketch-geometry (4):
    g0: LineSegment StartX=17.994 StartY=0 StartZ=0 EndX=-0.006037 EndY=0 EndZ=0
    g1: LineSegment StartX=-0.006037 StartY=0 StartZ=0 EndX=-0.006037 EndY=7.65336 EndZ=0
    g2: LineSegment StartX=-0.006037 StartY=7.65336 StartZ=0 EndX=17.994 EndY=7.65336 EndZ=0
    g3: LineSegment StartX=17.994 StartY=7.65336 StartZ=0 EndX=17.994 EndY=0 EndZ=0
  constraints (10):
    c: Coincident(g0,g1)
    c: Coincident(g1,g2)
    c: Coincident(g2,g3)
    c: Coincident(g3,g0)
    c: Horizontal(g0)
    c: Horizontal(g2)
    c: Vertical(g1)
    c: Vertical(g3)
    c: PointOnObject(g0,g-1)
    c: DistanceX(g2,g2) = 18
FEATURE [PartDesign::Pad] Pad011
  BaseFeature = -> Pad010
  Direction = (0,0,1)
  Length = 3
  Length2 = 10
  Profile = -> Sketch025
  ReferenceAxis = -> Sketch025 [N_Axis]
  Reversed = true
  Type = 0
FEATURE [Sketcher::SketchObject] Sketch026
  FullyConstrained = false
  MapMode = 5
  Support = -> [XY_Plane004]
  sketch-geometry (4):
    g0: LineSegment StartX=18.4065 StartY=12.5825 StartZ=0 EndX=20.7303 EndY=12.5825 EndZ=0
    g1: LineSegment StartX=20.7303 StartY=12.5825 StartZ=0 EndX=20.7303 EndY=10.153 EndZ=0
    g2: LineSegment StartX=20.7303 StartY=10.153 StartZ=0 EndX=18.4065 EndY=10.153 EndZ=0
    g3: LineSegment StartX=18.4065 StartY=10.153 StartZ=0 EndX=18.4065 EndY=12.5825 EndZ=0
  constraints (8):
    c: Coincident(g0,g1)
    c: Coincident(g1,g2)
    c: Coincident(g2,g3)
    c: Coincident(g3,g0)
    c: Horizontal(g0)
    c: Horizontal(g2)
    c: Vertical(g1)
    c: Vertical(g3)
FEATURE [PartDesign::Pad] Pad012
  BaseFeature = -> Pad011
  Direction = (0,0,1)
  Length = 5
  Length2 = 10
  Profile = -> Sketch026
  ReferenceAxis = -> Sketch026 [N_Axis]
  Type = 0
FEATURE [Sketcher::SketchObject] Sketch027
  ExternalGeometry = -> [Sketch026]
  FullyConstrained = true
  MapMode = 5
  Support = -> [XY_Plane004]
  sketch-geometry (3):
    g0: LineSegment StartX=18.4065 StartY=12.5825 StartZ=0 EndX=20.7303 EndY=10.153 EndZ=0
    g1: LineSegment StartX=20.7303 StartY=12.5825 StartZ=0 EndX=18.4065 EndY=10.153 EndZ=0
    g2: Circle CenterX=19.5684 CenterY=11.3678 CenterZ=0 NormalX=0 NormalY=0 NormalZ=1 AngleXU=0 Radius=0.25
  constraints (7):
    c: Coincident(g0,g-4)
    c: Coincident(g0,g-3)
    c: Coincident(g1,g-4)
    c: Coincident(g1,g-3)
    c: PointOnObject(g2,g0)
    c: PointOnObject(g2,g1)
    c: Diameter(g2) = 0.5
FEATURE [PartDesign::Pad] Pad013
  BaseFeature = -> Pad012
  Direction = (0,0,1)
  Length = 10
  Length2 = 10
  Profile = -> Sketch027
  ReferenceAxis = -> Sketch027 [N_Axis]
  Type = 0
FEATURE [PartDesign::Mirrored] Mirrored007
  BaseFeature = -> Pad013
  MirrorPlane = -> Sketch024 [H_Axis]
  Originals = -> [Pad010,Pad011]
FEATURE [PartDesign::Mirrored] Mirrored008
  MirrorPlane = -> Sketch026 [H_Axis]
FEATURE [PartDesign::LinearPattern] LinearPattern
  Direction = -> Sketch026 [H_Axis]
  Length = 35
  Occurrences = 15
  Reversed = true
FEATURE [PartDesign::MultiTransform] MultiTransform002
  BaseFeature = -> Mirrored007
  Originals = -> [Pad012,Pad013]
  Transformations = -> [Mirrored008,LinearPattern]
FEATURE [PartDesign::Body] Body004  label="esp001"
  Group = -> [Sketch024,Pad010,Sketch025,Pad011,Sketch026,Pad012,Sketch027,Pad013,Mirrored007,MultiTransform002,Mirrored008,LinearPattern]
  Origin = -> Origin004
  Placement = pos=(49,0,-16) rot=(0,0,1;0rad)
  Tip = -> MultiTransform002
FEATURE [Sketcher::SketchObject] Sketch028
  ExternalGeometry = -> [MultiTransform]
  FullyConstrained = true
  MapMode = 5
  Placement = pos=(0,0,28) rot=(1,0,0;3.14159rad)
  Support = -> [MultiTransform]
  sketch-geometry (9):
    g0: LineSegment StartX=15.5 StartY=32 StartZ=0 EndX=17.5 EndY=32 EndZ=0
    g1: LineSegment StartX=17.5 StartY=32 StartZ=0 EndX=17.5 EndY=-32 EndZ=0
    g2: LineSegment StartX=17.5 StartY=-32 StartZ=0 EndX=15.5 EndY=-32 EndZ=0
    g3: LineSegment StartX=15.5 StartY=-32 StartZ=0 EndX=15.5 EndY=32 EndZ=0
    g4: LineSegment StartX=-17.5 StartY=-32 StartZ=0 EndX=-15.5 EndY=-32 EndZ=0
    g5: LineSegment StartX=-15.5 StartY=-32 StartZ=0 EndX=-15.5 EndY=32 EndZ=0
    g6: LineSegment StartX=-15.5 StartY=32 StartZ=0 EndX=-17.5 EndY=32 EndZ=0
    g7: LineSegment StartX=-17.5 StartY=32 StartZ=0 EndX=-17.5 EndY=-32 EndZ=0
    g8: LineSegment StartX=-15.5 StartY=0 StartZ=0 EndX=15.5 EndY=0 EndZ=0
  constraints (27):
    c: Coincident(g0,g1)
    c: Coincident(g1,g2)
    c: Coincident(g2,g3)
    c: Coincident(g3,g0)
    c: Horizontal(g0)
    c: Horizontal(g2)
    c: Vertical(g1)
    c: Vertical(g3)
    c: PointOnObject(g0,g-4)
    c: PointOnObject(g1,g-5)
    c: Coincident(g4,g5)
    c: Coincident(g5,g6)
    c: Coincident(g6,g7)
    c: Coincident(g7,g4)
    c: Horizontal(g4)
    c: Horizontal(g6)
    c: Vertical(g5)
    c: Vertical(g7)
    c: PointOnObject(g4,g-5)
    c: PointOnObject(g5,g-4)
    c: Equal(g6,g0)
    c: DistanceX(g0,g0) = 2
    c: PointOnObject(g8,g5)
    c: PointOnObject(g8,g3)
    c: Horizontal(g8)
    c: Symmetric(g8,g8,g-3)
    c: DistanceX(g8,g8) = 31
FEATURE [PartDesign::Pad] Pad014
  BaseFeature = -> MultiTransform
  Direction = (0,0,-1)
  Length = 1
  Length2 = 10
  Profile = -> Sketch028
  ReferenceAxis = -> Sketch028 [N_Axis]
  Type = 0
FEATURE [Sketcher::SketchObject] Sketch030
  ExternalGeometry = -> [Sketch007]
  FullyConstrained = true
  MapMode = 5
  Support = -> [XY_Plane005]
  sketch-geometry (10):
    g0: ArcOfCircle CenterX=53.3345 CenterY=23 CenterZ=0 NormalX=0 NormalY=0 NormalZ=1 AngleXU=0 Radius=3.6 StartAngle=1.5708 EndAngle=4.71239
    g1: ArcOfCircle CenterX=58.1345 CenterY=23 CenterZ=0 NormalX=0 NormalY=0 NormalZ=1 AngleXU=0 Radius=3.6 StartAngle=4.71239 EndAngle=7.85398
    g2: LineSegment StartX=53.3345 StartY=19.4 StartZ=0 EndX=58.1345 EndY=19.4 EndZ=0
    g3: LineSegment StartX=58.1345 StartY=26.6 StartZ=0 EndX=53.3345 EndY=26.6 EndZ=0
    g4: LineSegment StartX=49.7345 StartY=26.6 StartZ=0 EndX=61.7345 EndY=26.6 EndZ=0
    g5: LineSegment StartX=61.7345 StartY=26.6 StartZ=0 EndX=61.7345 EndY=19.4 EndZ=0
    g6: LineSegment StartX=61.7345 StartY=19.4 StartZ=0 EndX=49.7345 EndY=19.4 EndZ=0
    g7: LineSegment StartX=49.7345 StartY=19.4 StartZ=0 EndX=49.7345 EndY=26.6 EndZ=0
    g8: LineSegment StartX=58.1345 StartY=23 StartZ=0 EndX=77.4691 EndY=50.7535 EndZ=0
    g9: LineSegment StartX=53.3345 StartY=23 StartZ=0 EndX=34 EndY=50.7535 EndZ=0
  constraints (26):
    c: Tangent(g0,g2) = -1.5708
    c: Tangent(g2,g1) = -1.5708
    c: Tangent(g1,g3) = -1.5708
    c: Tangent(g3,g0) = -1.5708
    c: Equal(g0,g1)
    c: Horizontal(g2)
    c: Coincident(g4,g5)
    c: Coincident(g5,g6)
    c: Coincident(g6,g7)
    c: Coincident(g7,g4)
    c: Horizontal(g4)
    c: Horizontal(g6)
    c: Vertical(g5)
    c: Vertical(g7)
    c: Tangent(g5,g1)
    c: Tangent(g7,g0)
    c: PointOnObject(g0,g4)
    c: PointOnObject(g0,g6)
    c: DistanceY(g5,g5) = 7.2
    c: DistanceX(g6,g6) = 12
    c: Coincident(g8,g1)
    c: Coincident(g8,g-5)
    c: Coincident(g9,g0)
    c: Coincident(g9,g-5)
    c: Equal(g8,g9)
    c: DistanceY(g-1,g1) = 23
FEATURE [Sketcher::SketchObject] Sketch031
  ExternalGeometry = -> [Sketch013,Sketch018]
  FullyConstrained = false
  MapMode = 5
  Support = -> [XY_Plane005]
  sketch-geometry (6):
    g0: Circle CenterX=66.5863 CenterY=23 CenterZ=0 NormalX=0 NormalY=0 NormalZ=1 AngleXU=0 Radius=1.5
    g1: Circle CenterX=44.8828 CenterY=23 CenterZ=0 NormalX=0 NormalY=0 NormalZ=1 AngleXU=0 Radius=1.5
    g2: LineSegment StartX=44.8828 StartY=23 StartZ=0 EndX=66.5863 EndY=23 EndZ=0
    g3: LineSegment StartX=53.3345 StartY=26.6 StartZ=0 EndX=58.1345 EndY=19.4 EndZ=0
    g4: LineSegment StartX=53.3345 StartY=19.4 StartZ=0 EndX=58.1345 EndY=26.6 EndZ=0
    g5: GeomPoint X=55.7345 Y=23 Z=0
  constraints (12):
    c: Equal(g1,g-3)
    c: Equal(g-3,g0)
    c: Coincident(g2,g1)
    c: Coincident(g2,g0)
    c: PointOnObject(g-5,g2)
    c: Coincident(g3,g-4)
    c: Coincident(g3,g-5)
    c: Coincident(g4,g-4)
    c: Coincident(g4,g-5)
    c: Symmetric(g0,g1,g5)
    c: PointOnObject(g-4,g2)
    c: PointOnObject(g5,g3)
FEATURE [Sketcher::SketchObject] Sketch033
  FullyConstrained = false
  MapMode = 5
  Support = -> [XY_Plane005]
  sketch-geometry (8):
    g0: LineSegment StartX=-34 StartY=34 StartZ=0 EndX=34 EndY=34 EndZ=0
    g1: LineSegment StartX=34 StartY=-34 StartZ=0 EndX=-34 EndY=-34 EndZ=0
    g2: LineSegment StartX=-34 StartY=-34 StartZ=0 EndX=-34 EndY=34 EndZ=0
    g3: LineSegment StartX=34 StartY=50.7535 StartZ=0 EndX=77.4691 EndY=50.7535 EndZ=0
    g4: LineSegment StartX=77.4691 StartY=50.7535 StartZ=0 EndX=77.4691 EndY=-50.7535 EndZ=0
    g5: LineSegment StartX=77.4691 StartY=-50.7535 StartZ=0 EndX=34 EndY=-50.7535 EndZ=0
    g6: LineSegment StartX=34 StartY=34 StartZ=0 EndX=34 EndY=50.7535 EndZ=0
    g7: LineSegment StartX=34 StartY=-34 StartZ=0 EndX=34 EndY=-50.7535 EndZ=0
  constraints (21):
    c: Coincident(g1,g2)
    c: Coincident(g2,g0)
    c: Horizontal(g0)
    c: Horizontal(g1)
    c: Vertical(g2)
    c: Coincident(g3,g4)
    c: Coincident(g4,g5)
    c: Horizontal(g3)
    c: Horizontal(g5)
    c: Vertical(g4)
    c: Coincident(g6,g0)
    c: Coincident(g6,g3)
    c: Vertical(g6)
    c: Coincident(g7,g1)
    c: Coincident(g7,g5)
    c: Vertical(g7)
    c: Equal(g6,g7)
    c: Symmetric(g1,g0,g-1)
    c: DistanceY(g2,g2) = 68
    c: Equal(g1,g2)
    c: Equal(g3,g5)
FEATURE [Sketcher::SketchObject] Sketch029
  ExternalGeometry = -> [Sketch030,Sketch031,Sketch033]
  FullyConstrained = false
  MapMode = 5
  Placement = pos=(0,0,0) rot=(1,0,0;1.5708rad)
  Support = -> [XZ_Plane005]
  sketch-geometry (11):
    g0: LineSegment StartX=77.4691 StartY=5.1e-15 StartZ=0 EndX=77.4691 EndY=-25 EndZ=0
    g1: LineSegment StartX=38.3828 StartY=-15 StartZ=0 EndX=38.3828 EndY=0 EndZ=0
    g2: LineSegment StartX=-24.2907 StartY=-15 StartZ=0 EndX=-24.2907 EndY=-25 EndZ=0
    g3: LineSegment StartX=-24.2907 StartY=-25 StartZ=0 EndX=77.4691 EndY=-25 EndZ=0
    g4: LineSegment StartX=-24.2907 StartY=-15 StartZ=0 EndX=38.3828 EndY=-15 EndZ=0
    g5: LineSegment StartX=38.3828 StartY=0 StartZ=0 EndX=49.7345 EndY=5.3e-15 EndZ=0
    g6: LineSegment StartX=77.4691 StartY=5.1e-15 StartZ=0 EndX=61.7345 EndY=5.1e-15 EndZ=0
    g7: LineSegment StartX=61.7345 StartY=5.1e-15 StartZ=0 EndX=61.7345 EndY=-7.5 EndZ=0
    g8: LineSegment StartX=61.7345 StartY=-7.5 StartZ=0 EndX=49.7345 EndY=-7.5 EndZ=0
    g9: LineSegment StartX=49.7345 StartY=-7.5 StartZ=0 EndX=49.7345 EndY=5.3e-15 EndZ=0
    g10: LineSegment StartX=49.7345 StartY=-7.5 StartZ=0 EndX=38.3828 EndY=-7.5 EndZ=0
  constraints (29):
    c: Vertical(g0)
    c: PointOnObject(g1,g-1)
    c: Coincident(g2,g3)
    c: Horizontal(g3)
    c: Vertical(g2)
    c: Coincident(g4,g2)
    c: Coincident(g4,g1)
    c: Horizontal(g4)
    c: Coincident(g5,g1)
    c: Coincident(g5,g-4)
    c: Coincident(g6,g0)
    c: Coincident(g6,g-5)
    c: Coincident(g0,g3)
    c: Coincident(g7,g8)
    c: Coincident(g8,g9)
    c: Horizontal(g8)
    c: Vertical(g7)
    c: Vertical(g9)
    c: Coincident(g7,g6)
    c: Coincident(g10,g8)
    c: Symmetric(g1,g1,g10)
    c: Coincident(g9,g5)
    c: Horizontal(g10)
    c: Vertical(g1)
    c: DistanceY(g1,g1) = 15
    c: DistanceY(g2,g2) = 10
    c: DistanceX(g-7,g5) = 3.35171
    c: DistanceX(g1,g-7) = 5
    c: Coincident(g0,g-8)
FEATURE [PartDesign::Pad] Pad015
  Direction = (0,-1,2e-16)
  Length = 12
  Length2 = 10
  Placement = pos=(0,0,0) rot=(1,0,0;1.5708rad)
  Profile = -> Sketch029
  ReferenceAxis = -> Sketch029 [N_Axis]
  Type = 0
FEATURE [Sketcher::SketchObject] Sketch032
  ExternalGeometry = -> [Sketch031,Pad015]
  FullyConstrained = true
  MapMode = 5
  Support = -> [XY_Plane005]
  sketch-geometry (8):
    g0: Circle CenterX=44.8828 CenterY=-6 CenterZ=0 NormalX=0 NormalY=0 NormalZ=1 AngleXU=0 Radius=1.5
    g1: Circle CenterX=66.5863 CenterY=-6 CenterZ=0 NormalX=0 NormalY=0 NormalZ=1 AngleXU=0 Radius=1.5
    g2: LineSegment StartX=44.8828 StartY=-6 StartZ=0 EndX=44.8828 EndY=23 EndZ=0
    g3: LineSegment StartX=44.8828 StartY=23 StartZ=0 EndX=66.5863 EndY=23 EndZ=0
    g4: LineSegment StartX=66.5863 StartY=23 StartZ=0 EndX=66.5863 EndY=-6 EndZ=0
    g5: LineSegment StartX=66.5863 StartY=-6 StartZ=0 EndX=44.8828 EndY=-6 EndZ=0
    g6: GeomPoint X=55.7345 Y=8.5 Z=0
    g7: GeomPoint X=49.7345 Y=-6 Z=0
  constraints (16):
    c: Equal(g1,g0)
    c: Equal(g0,g-3)
    c: Coincident(g2,g3)
    c: Coincident(g3,g4)
    c: Coincident(g4,g5)
    c: Coincident(g5,g2)
    c: Vertical(g2)
    c: Vertical(g4)
    c: Symmetric(g3,g2,g6)
    c: Coincident(g3,g-4)
    c: Coincident(g4,g1)
    c: Coincident(g2,g-3)
    c: Coincident(g0,g2)
    c: Horizontal(g5)
    c: PointOnObject(g7,g5)
    c: Symmetric(g-5,g-7,g7)
FEATURE [PartDesign::Pocket] Pocket013
  BaseFeature = -> Pad015
  Direction = (0,0,-1)
  Length = 5
  Length2 = 5
  Placement = pos=(0,0,0) rot=(1,0,0;1.5708rad)
  Profile = -> Sketch032
  ReferenceAxis = -> Sketch032 [N_Axis]
  Type = 1
FEATURE [Sketcher::SketchObject] Sketch034
  ExternalGeometry = -> [Pocket013]
  FullyConstrained = false
  MapMode = 5
  Support = -> [XY_Plane005]
  sketch-geometry (3):
    g0: LineSegment StartX=-24.2907 StartY=-6 StartZ=0 EndX=66.5863 EndY=-6 EndZ=0
    g1: Circle CenterX=-5.78794 CenterY=-6 CenterZ=0 NormalX=0 NormalY=0 NormalZ=1 AngleXU=0 Radius=2.55
    g2: Circle CenterX=20.4831 CenterY=-6 CenterZ=0 NormalX=0 NormalY=0 NormalZ=1 AngleXU=0 Radius=2.55
  constraints (7):
    c: Coincident(g0,g-4)
    c: Horizontal(g0)
    c: PointOnObject(g0,g-5)
    c: PointOnObject(g1,g0)
    c: PointOnObject(g2,g0)
    c: Equal(g2,g1)
    c: Diameter(g1) = 5.1
FEATURE [PartDesign::Pocket] Pocket014
  BaseFeature = -> Pocket013
  Direction = (0,0,-1)
  Length = 5
  Length2 = 5
  Placement = pos=(0,0,0) rot=(1,0,0;1.5708rad)
  Profile = -> Sketch034
  ReferenceAxis = -> Sketch034 [N_Axis]
  Type = 1
FEATURE [Sketcher::SketchObject] Sketch035
  ExternalGeometry = -> [Pocket014]
  FullyConstrained = true
  MapMode = 5
  Placement = pos=(0,-1.1e-14,-25) rot=(1,0,0;3.14159rad)
  Support = -> [Pocket014]
  sketch-geometry (14):
    g0: LineSegment StartX=46.586 StartY=8.95 StartZ=0 EndX=43.1797 EndY=8.95 EndZ=0
    g1: LineSegment StartX=43.1797 StartY=8.95 StartZ=0 EndX=41.4765 EndY=6 EndZ=0
    g2: LineSegment StartX=41.4765 StartY=6 StartZ=0 EndX=43.1797 EndY=3.05 EndZ=0
    g3: LineSegment StartX=43.1797 StartY=3.05 StartZ=0 EndX=46.586 EndY=3.05 EndZ=0
    g4: LineSegment StartX=46.586 StartY=3.05 StartZ=0 EndX=48.2892 EndY=6 EndZ=0
    g5: LineSegment StartX=48.2892 StartY=6 StartZ=0 EndX=46.586 EndY=8.95 EndZ=0
    g6: Circle CenterX=44.8828 CenterY=6 CenterZ=0 NormalX=0 NormalY=0 NormalZ=1 AngleXU=0 Radius=3.40637
    g7: LineSegment StartX=68.2894 StartY=8.95 StartZ=0 EndX=64.8831 EndY=8.95 EndZ=0
    g8: LineSegment StartX=64.8831 StartY=8.95 StartZ=0 EndX=63.1799 EndY=6 EndZ=0
    g9: LineSegment StartX=63.1799 StartY=6 StartZ=0 EndX=64.8831 EndY=3.05 EndZ=0
    g10: LineSegment StartX=64.8831 StartY=3.05 StartZ=0 EndX=68.2894 EndY=3.05 EndZ=0
    g11: LineSegment StartX=68.2894 StartY=3.05 StartZ=0 EndX=69.9926 EndY=6 EndZ=0
    g12: LineSegment StartX=69.9926 StartY=6 StartZ=0 EndX=68.2894 EndY=8.95 EndZ=0
    g13: Circle CenterX=66.5863 CenterY=6 CenterZ=0 NormalX=0 NormalY=0 NormalZ=1 AngleXU=0 Radius=3.40637
  constraints (32):
    c: Coincident(g0,g1)
    c: Coincident(g1,g2)
    c: Coincident(g2,g3)
    c: Coincident(g3,g4)
    c: Coincident(g4,g5)
    c: Coincident(g5,g0)
    c: Equal(g0, g1-g5) x5
    c: PointOnObject(g0,g6)
    c: PointOnObject(g1,g6)
    c: PointOnObject(g2,g6)
    c: PointOnObject(g3,g6)
    c: PointOnObject(g4,g6)
    c: PointOnObject(g5,g6)
    c: Coincident(g6,g-3)
    c: Coincident(g7,g8)
    c: Coincident(g8,g9)
    c: Coincident(g9,g10)
    c: Coincident(g10,g11)
    c: Coincident(g11,g12)
    c: Coincident(g12,g7)
    c: Equal(g7, g8-g12) x5
    c: PointOnObject(g7,g13)
    c: PointOnObject(g8,g13)
    c: PointOnObject(g9,g13)
    c: PointOnObject(g10,g13)
    c: PointOnObject(g11,g13)
    c: PointOnObject(g12,g13)
    c: Coincident(g13,g-4)
    c: Horizontal(g7)
    c: Horizontal(g0)
    c: Equal(g6,g13)
    c: DistanceY(g10,g7) = 5.9
FEATURE [PartDesign::Pocket] Pocket015
  BaseFeature = -> Pocket014
  Direction = (0,7e-16,1)
  Length = 15
  Length2 = 5
  Placement = pos=(0,0,0) rot=(1,0,0;1.5708rad)
  Profile = -> Sketch035
  ReferenceAxis = -> Sketch035 [N_Axis]
  Type = 0
FEATURE [Sketcher::SketchObject] Sketch036
  ExternalGeometry = -> [Pocket015]
  FullyConstrained = true
  MapMode = 5
  Placement = pos=(0,-6.6e-15,-15) rot=(0,0,1;3.14159rad)
  Support = -> [Pocket015]
  sketch-geometry (14):
    g0: LineSegment StartX=-22.9369 StartY=10.25 StartZ=0 EndX=-25.3906 EndY=6 EndZ=0
    g1: LineSegment StartX=-25.3906 StartY=6 StartZ=0 EndX=-22.9369 EndY=1.75 EndZ=0
    g2: LineSegment StartX=-22.9369 StartY=1.75 StartZ=0 EndX=-18.0294 EndY=1.75 EndZ=0
    g3: LineSegment StartX=-18.0294 StartY=1.75 StartZ=0 EndX=-15.5757 EndY=6 EndZ=0
    g4: LineSegment StartX=-15.5757 StartY=6 StartZ=0 EndX=-18.0294 EndY=10.25 EndZ=0
    g5: LineSegment StartX=-18.0294 StartY=10.25 StartZ=0 EndX=-22.9369 EndY=10.25 EndZ=0
    g6: Circle CenterX=-20.4831 CenterY=6 CenterZ=0 NormalX=0 NormalY=0 NormalZ=1 AngleXU=0 Radius=4.90748
    g7: LineSegment StartX=3.33421 StartY=10.25 StartZ=0 EndX=0.880467 EndY=6 EndZ=0
    g8: LineSegment StartX=0.880467 StartY=6 StartZ=0 EndX=3.33421 EndY=1.75 EndZ=0
    g9: LineSegment StartX=3.33421 StartY=1.75 StartZ=0 EndX=8.24168 EndY=1.75 EndZ=0
    g10: LineSegment StartX=8.24168 StartY=1.75 StartZ=0 EndX=10.6954 EndY=6 EndZ=0
    g11: LineSegment StartX=10.6954 StartY=6 StartZ=0 EndX=8.24168 EndY=10.25 EndZ=0
    g12: LineSegment StartX=8.24168 StartY=10.25 StartZ=0 EndX=3.33421 EndY=10.25 EndZ=0
    g13: Circle CenterX=5.78794 CenterY=6 CenterZ=0 NormalX=0 NormalY=0 NormalZ=1 AngleXU=0 Radius=4.90748
  constraints (32):
    c: Coincident(g0,g1)
    c: Coincident(g1,g2)
    c: Coincident(g2,g3)
    c: Coincident(g3,g4)
    c: Coincident(g4,g5)
    c: Coincident(g5,g0)
    c: Equal(g0, g1-g5) x5
    c: PointOnObject(g0,g6)
    c: PointOnObject(g1,g6)
    c: PointOnObject(g2,g6)
    c: PointOnObject(g3,g6)
    c: PointOnObject(g4,g6)
    c: PointOnObject(g5,g6)
    c: Coincident(g7,g8)
    c: Coincident(g8,g9)
    c: Coincident(g9,g10)
    c: Coincident(g10,g11)
    c: Coincident(g11,g12)
    c: Coincident(g12,g7)
    c: Equal(g7, g8-g12) x5
    c: PointOnObject(g7,g13)
    c: PointOnObject(g8,g13)
    c: PointOnObject(g9,g13)
    c: PointOnObject(g10,g13)
    c: PointOnObject(g11,g13)
    c: PointOnObject(g12,g13)
    c: Horizontal(g12)
    c: Horizontal(g5)
    c: Equal(g13,g6)
    c: DistanceY(g9,g11) = 8.5
    c: Coincident(g6,g-8)
    c: Coincident(g13,g-7)
FEATURE [PartDesign::Pocket] Pocket016
  BaseFeature = -> Pocket015
  Direction = (0,-8e-16,-1)
  Length = 4
  Length2 = 5
  Placement = pos=(0,0,0) rot=(1,0,0;1.5708rad)
  Profile = -> Sketch036
  ReferenceAxis = -> Sketch036 [N_Axis]
  Type = 0
FEATURE [PartDesign::Fillet] Fillet
  Base = -> Pocket016 [Edge2]
  BaseFeature = -> Pocket016
  Placement = pos=(0,0,0) rot=(1,0,0;1.5708rad)
  Radius = 5
  SupportTransform = false
  UseAllEdges = false
FEATURE [PartDesign::Body] Body005  label="clamp"
  Group = -> [Sketch029,Sketch030,Sketch031,Pad015,Sketch032,Pocket013,Sketch033,Sketch034,Pocket014,Sketch035,Pocket015,Sketch036,Pocket016,Fillet]
  Origin = -> Origin005
  Placement = pos=(0,29,-22) rot=(0,0,1;0rad)
  Tip = -> Fillet
FEATURE [PartDesign::Chamfer] Chamfer
  Angle = 45
  Base = -> Pad014 [Edge77]
  BaseFeature = -> Pad014
  ChamferType = 0
  FlipDirection = false
  Size = 3.6
  Size2 = 1
  SupportTransform = false
  UseAllEdges = false
FEATURE [PartDesign::Fillet] Fillet001
  Base = -> Chamfer [Edge97,Edge81,Edge86,Edge96,Edge99,Edge102,Edge103]
  BaseFeature = -> Chamfer
  Radius = 5.5
  SupportTransform = false
  UseAllEdges = false
FEATURE [PartDesign::Mirrored] Mirrored009
  BaseFeature = -> Fillet001
  MirrorPlane = -> XZ_Plane
  Originals = -> [Chamfer,Fillet001]
FEATURE [PartDesign::Fillet] Fillet002
  Base = -> Mirrored009 [Edge68]
  BaseFeature = -> Mirrored009
  Radius = 5
  SupportTransform = false
  UseAllEdges = false
FEATURE [PartDesign::Chamfer] Chamfer001
  Angle = 45
  Base = -> Mirrored005 [Edge178]
  BaseFeature = -> Mirrored005
  ChamferType = 0
  FlipDirection = false
  Size = 3.6
  Size2 = 1
  SupportTransform = false
  UseAllEdges = false
FEATURE [PartDesign::Fillet] Fillet003
  Base = -> Chamfer001 [Edge139,Edge137,Edge135,Edge133,Edge95,Edge112]
  BaseFeature = -> Chamfer001
  Radius = 6
  SupportTransform = false
  UseAllEdges = false
FEATURE [PartDesign::Chamfer] Chamfer002
  Angle = 45
  Base = -> Fillet003 [Edge58,Edge73,Edge81]
  BaseFeature = -> Fillet003
  ChamferType = 0
  FlipDirection = false
  Size = 1
  Size2 = 1
  SupportTransform = false
  UseAllEdges = false
FEATURE [PartDesign::Mirrored] Mirrored010
  BaseFeature = -> Chamfer002
  MirrorPlane = -> XZ_Plane001
  Originals = -> [Chamfer002,Fillet003,Chamfer001]
FEATURE [PartDesign::Body] Body001  label="Bottom"
  Group = -> [Sketch007,Pad002,Thickness001,Sketch012,Pad003,Sketch013,Pocket009,Sketch014,Pocket010,MultiTransform001,Mirrored002,Mirrored003,Sketch015,Pad004,Sketch016,Pad005,Mirrored004,Sketch017,Pad006,Pocket011,Pocket012,Mirrored005,Sketch018,Sketch019,Chamfer001,Fillet003,Chamfer002,Mirrored010]
  Origin = -> Origin001
  Placement = pos=(0,0,-22) rot=(0,0,1;0rad)
  Tip = -> Mirrored010
FEATURE [Sketcher::SketchObject] Sketch037
  FullyConstrained = true
  MapMode = 5
  Placement = pos=(0,0,0) rot=(1,0,0;1.5708rad)
  Support = -> [XZ_Plane]
FEATURE [Sketcher::SketchObject] Sketch038
  FullyConstrained = true
  MapMode = 5
  Placement = pos=(0,0,0) rot=(0.57735,0.57735,0.57735;2.0944rad)
  Support = -> [YZ_Plane]
  sketch-geometry (1):
    g0: Circle CenterX=0 CenterY=0 CenterZ=0 NormalX=0 NormalY=0 NormalZ=1 AngleXU=0 Radius=3.25
  constraints (2):
    c: Coincident(g0,g-1)
    c: Diameter(g0) = 6.5
FEATURE [PartDesign::Pocket] Pocket017
  BaseFeature = -> Fillet002
  Direction = (-1,2e-16,-3e-16)
  Length = 50
  Length2 = 5
  Profile = -> Sketch038
  ReferenceAxis = -> Sketch038 [N_Axis]
  Type = 0
FEATURE [PartDesign::Body] Body  label="Top"
  Group = -> [Sketch,Pad,DatumPlane,Sketch001,Pocket,Thickness,Sketch002,Pocket001,Sketch003,Pocket002,Sketch004,Pocket003,Sketch005,Pad001,Sketch006,Pocket004,MultiTransform,Mirrored,Mirrored001,Sketch028,Pad014,Chamfer,Fillet001,Mirrored009,Fillet002,Sketch037,Sketch038,Pocket017]
  Origin = -> Origin
  Tip = -> Pocket017
